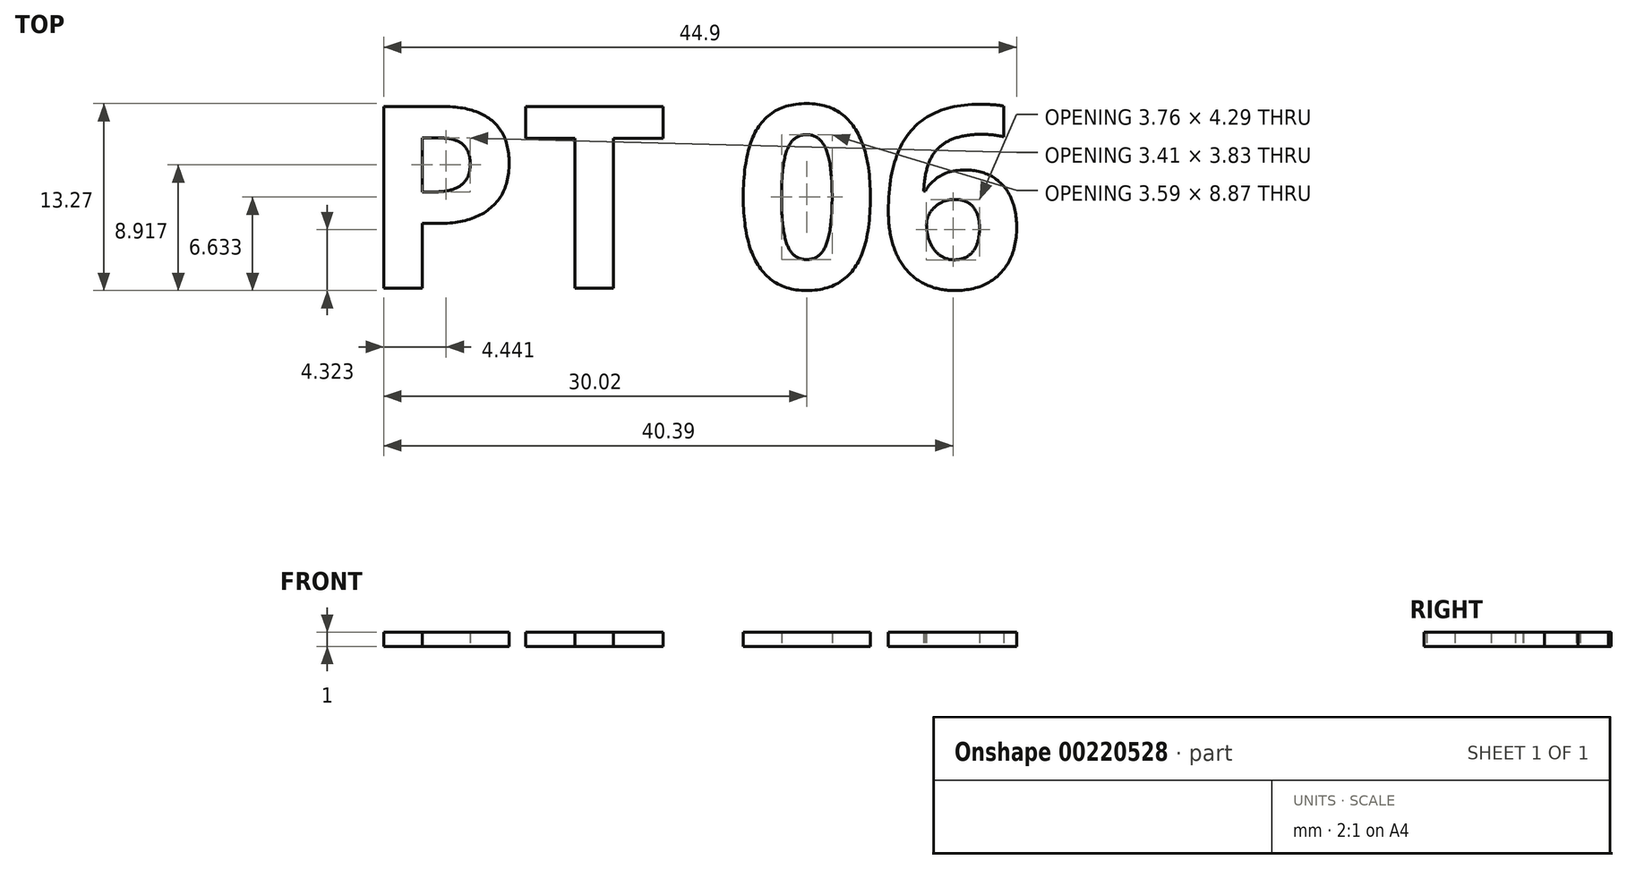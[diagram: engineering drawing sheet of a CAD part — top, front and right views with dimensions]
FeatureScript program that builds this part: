
annotation { "Feature Type Name" : "Feature", "Feature Type Description" : "" }
export const myFeature = defineFeature(function(context is Context, id is Id, definition is map)
    precondition{}
    {
        {
            var Q0;
            Q0=qCreatedBy(makeId("Top.planeOp"),FACE);
            var sketch = newSketch(context, id + "F0", { "sketchPlane" : qUnion([Q0])});
            skText(sketch, "E0", { "text": "PT 06", "fontName": "OpenSans-Bold.ttf"});
            const initialGuessF0  = {"E0": [-0.02385, -0.0065, 1, 0, 0.013]};
            skSetInitialGuess(sketch, initialGuessF0);
            skSolve(sketch);
        }
        {
            var Q0;
            Q0 = qSketchRegion(id + "F0", true);
            extrude(context, id + "F1", {"entities" : qUnion([Q0]), "depth" : 1 * mm});
        }
    });
